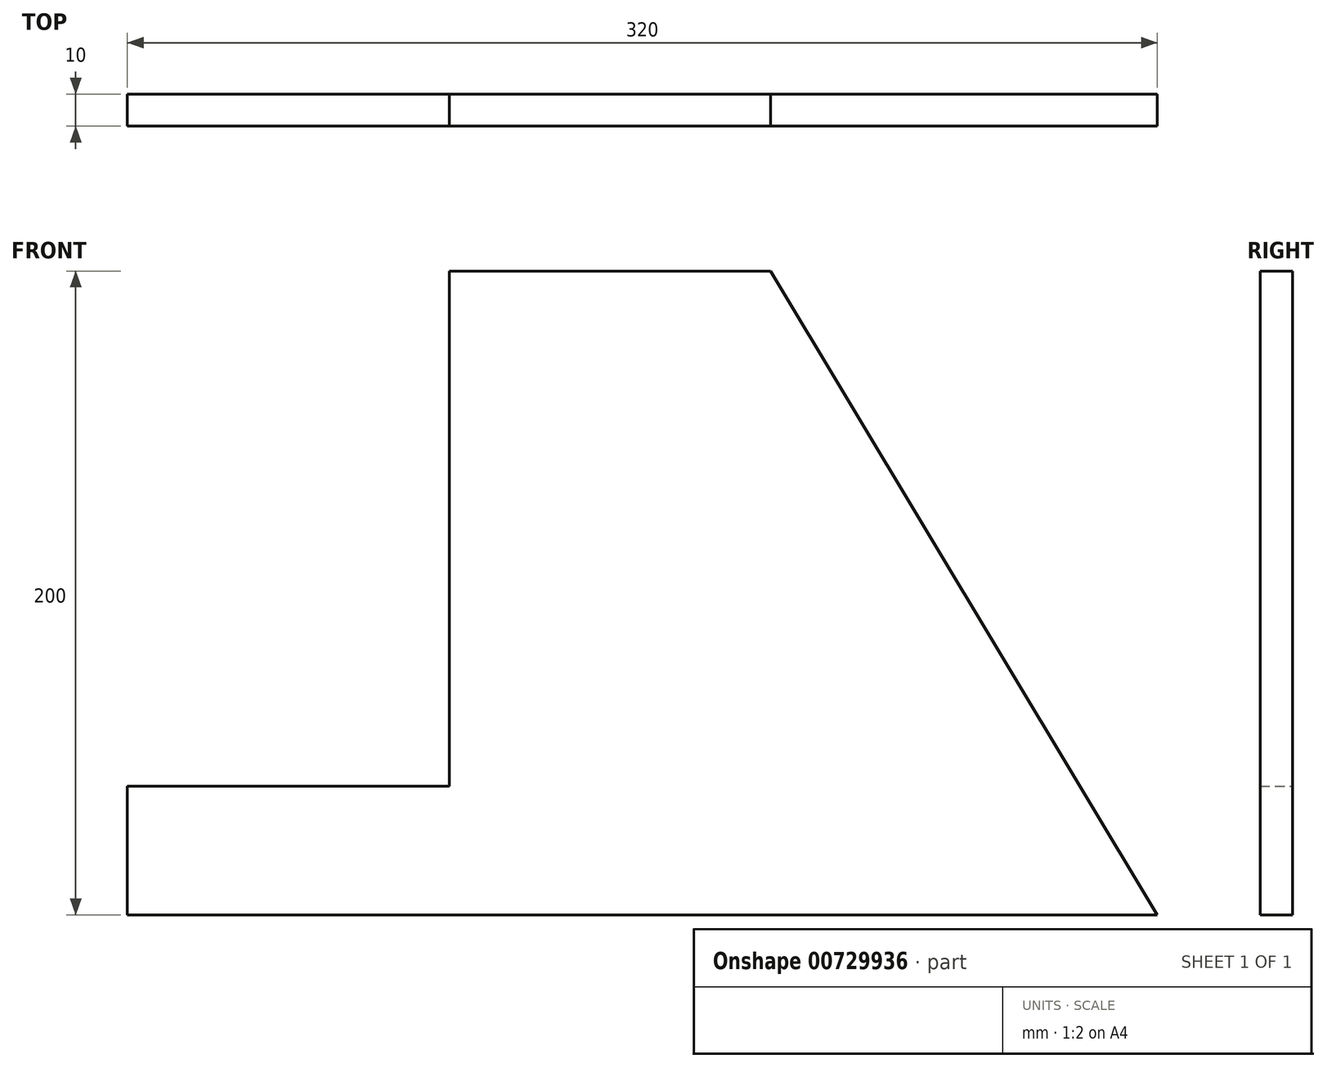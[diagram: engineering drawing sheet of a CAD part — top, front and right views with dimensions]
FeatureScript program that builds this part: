
annotation { "Feature Type Name" : "Feature", "Feature Type Description" : "" }
export const myFeature = defineFeature(function(context is Context, id is Id, definition is map)
    precondition{}
    {
        {
            var Q0;
            Q0=qCreatedBy(makeId("Front.planeOp"),FACE);
            var sketch = newSketch(context, id + "F0", { "sketchPlane" : qUnion([Q0])});
            skLineSegment(sketch, "E0", {"start": v(-48.42, -21.64) * mm, "end": v(-148.42, -21.64) * mm});
            skLineSegment(sketch, "E1", {"start": v(-148.42, -21.64) * mm, "end": v(-148.42, -61.64) * mm});
            skLineSegment(sketch, "E2", {"start": v(-148.42, -61.64) * mm, "end": v(171.58, -61.64) * mm});
            skLineSegment(sketch, "E3", {"start": v(51.4, 138.36) * mm, "end": v(-48.42, 138.36) * mm});
            skLineSegment(sketch, "E4", {"start": v(-48.42, 138.36) * mm, "end": v(-48.42, -21.64) * mm});
            skLineSegment(sketch, "E5", {"start": v(171.58, -61.64) * mm, "end": v(51.4, 138.36) * mm});
            skSolve(sketch);
        }
        {
            var Q0;
            Q0 = qSketchRegion(id + "F0", true);
            extrude(context, id + "F1", {"entities" : qUnion([Q0]), "depth" : 10 * mm, "offsetDistance" : 25 * mm});
        }
    });
